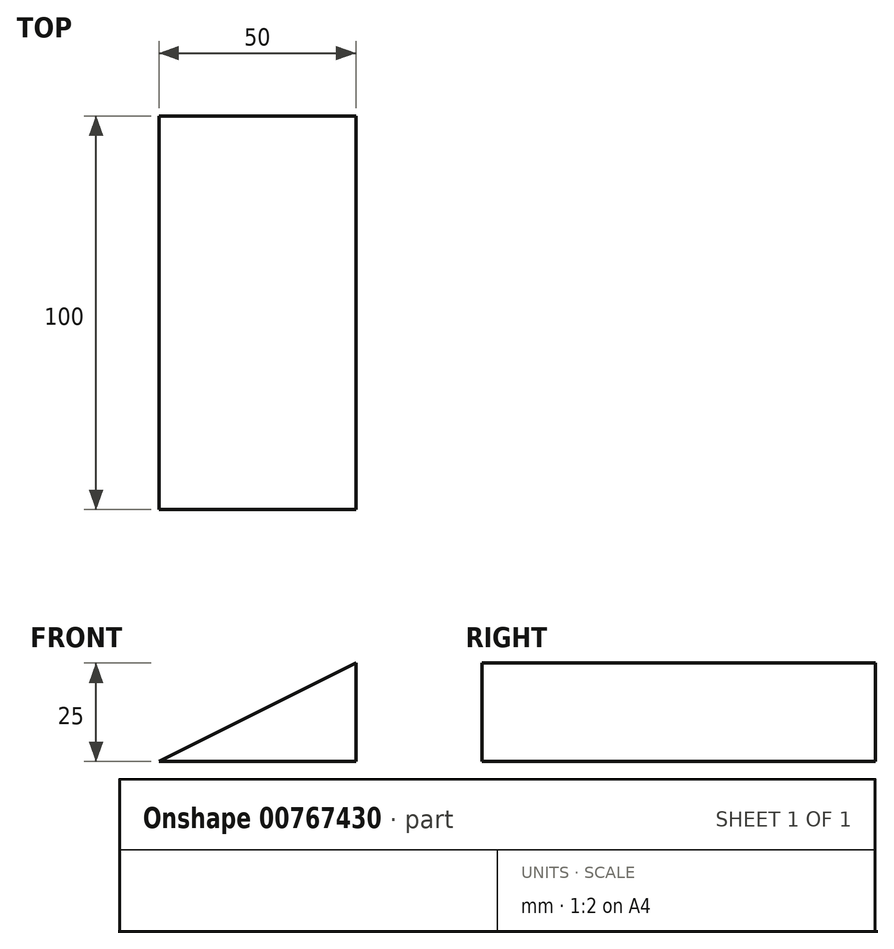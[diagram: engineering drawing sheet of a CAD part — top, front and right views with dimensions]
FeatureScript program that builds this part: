
annotation { "Feature Type Name" : "Feature", "Feature Type Description" : "" }
export const myFeature = defineFeature(function(context is Context, id is Id, definition is map)
    precondition{}
    {
        {
            var Q0;
            Q0=qCreatedBy(makeId("Front.planeOp"),FACE);
            var sketch = newSketch(context, id + "F0", { "sketchPlane" : qUnion([Q0])});
            skLineSegment(sketch, "E0", {"start": v(-25, -12.5) * mm, "end": v(25, -12.5) * mm});
            skLineSegment(sketch, "E1", {"start": v(25, -12.5) * mm, "end": v(25, 12.5) * mm});
            skLineSegment(sketch, "E2", {"start": v(25, 12.5) * mm, "end": v(-25, -12.5) * mm});
            skSolve(sketch);
        }
        {
            var Q0;
            Q0 = qSketchRegion(id + "F0", true);
            extrude(context, id + "F1", {"entities" : qUnion([Q0]), "endBound" : BoundingType.SYMMETRIC, "depth" : 100 * mm, "offsetDistance" : 25 * mm});
        }
    });
